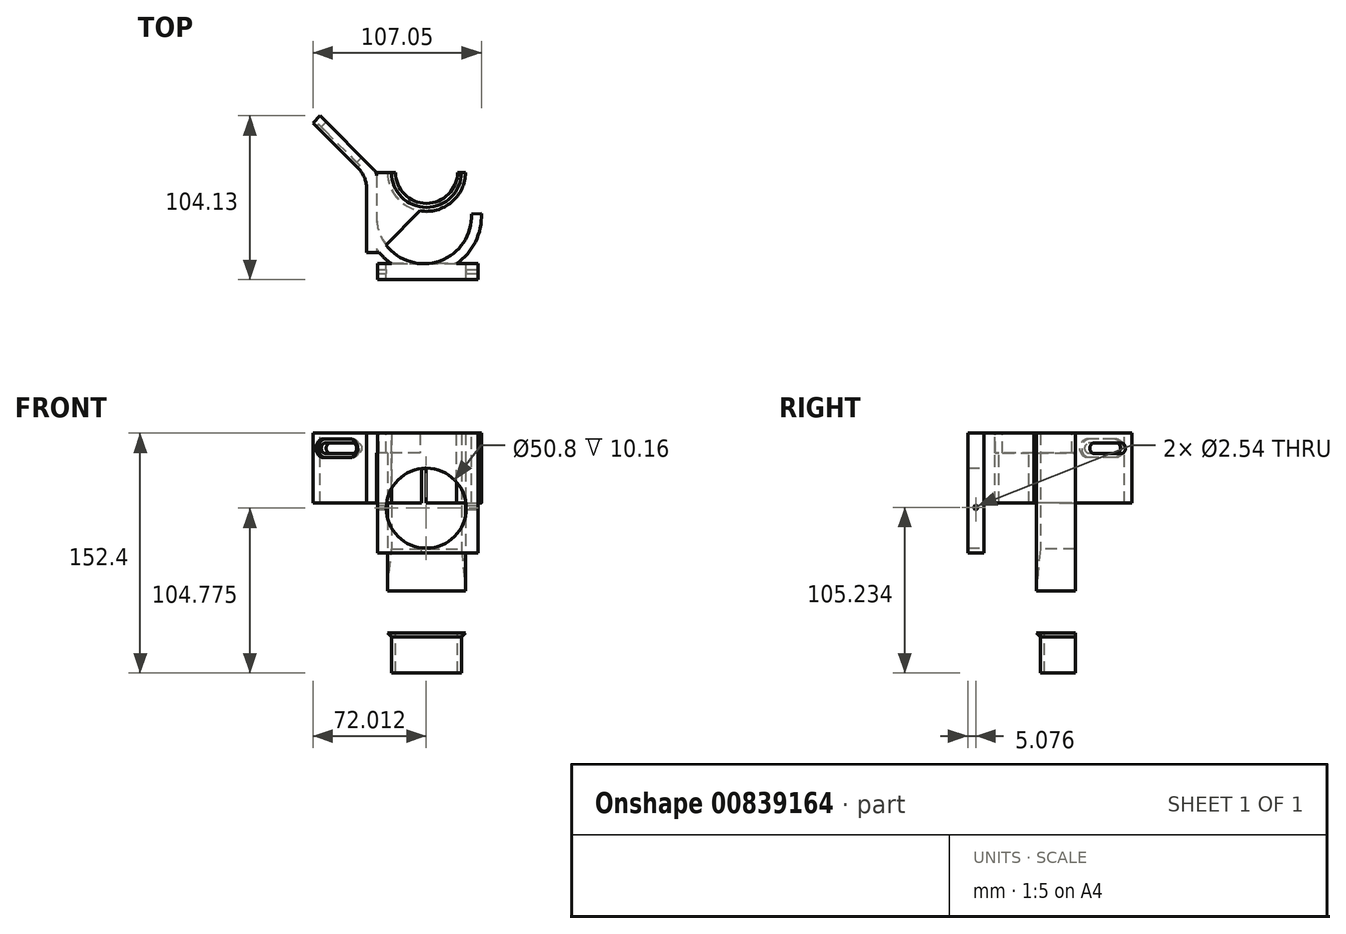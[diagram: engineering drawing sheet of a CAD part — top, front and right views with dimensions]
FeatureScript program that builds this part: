
annotation { "Feature Type Name" : "Feature", "Feature Type Description" : "" }
export const myFeature = defineFeature(function(context is Context, id is Id, definition is map)
    precondition{}
    {
        {
            var Q0;
            Q0=qCreatedBy(makeId("Top.planeOp"),FACE);
            var sketch = newSketch(context, id + "F0", { "sketchPlane" : qUnion([Q0])});
            skCircle(sketch, "E0", {"center": v(0, 0) * mm, "radius": 22.23 * mm});
            skCircle(sketch, "E1", {"center": v(0, 0) * mm, "radius": 24.77 * mm});
            skSolve(sketch);
        }
        {
            var Q0;
            Q0=makeQuery(id+"F0.imprint","IMPRINT",FACE,{"disambiguationData":[TD([[makeQuery(id+"F0.imprint","IMPRINT",EDGE,{"derivedFrom":sQuery(id+"F0.wireOp",EDGE,"E0")}),-1.0]])]});
            var sketch = newSketch(context, id + "F1", { "sketchPlane" : qUnion([Q0])});
            skSolve(sketch);
        }
        {
            var Q0;
            Q0=makeQuery(id+"F1.imprint","IMPRINT",FACE,{"disambiguationData":[TD([[makeQuery(id+"F1.imprint","IMPRINT",EDGE,{"derivedFrom":makeQuery(id+"F0.imprint","IMPRINT",EDGE,{"derivedFrom":sQuery(id+"F0.wireOp",EDGE,"E0")})}),-1.0]])]});
            extrude(context, id + "F2", {"entities" : qUnion([Q0]), "depth" : 127 * mm, "offsetDistance" : 25.4 * mm});
        }
        {
            var Q0;
            Q0=qCreatedBy(makeId("Top.planeOp"),FACE);
            var sketch = newSketch(context, id + "F3", { "sketchPlane" : qUnion([Q0])});
            skLineSegment(sketch, "E2.bottom", {"start": v(38.25, 0) * mm, "end": v(-119.23, 0) * mm});
            skLineSegment(sketch, "E2.top", {"start": v(38.25, 78.16) * mm, "end": v(-119.23, 78.16) * mm});
            skLineSegment(sketch, "E2.left", {"start": v(38.25, 0) * mm, "end": v(38.25, 78.16) * mm});
            skLineSegment(sketch, "E2.right", {"start": v(-119.23, 0) * mm, "end": v(-119.23, 78.16) * mm});
            skPoint(sketch, "E2.middle", {"position": v(-40.5, 39.08) * mm});
            skSolve(sketch);
        }
        {
            var Q0;
            Q0=makeQuery(id+"F3.imprint","IMPRINT",FACE,{"disambiguationData":[TD([[makeQuery(id+"F3.imprint","IMPRINT",EDGE,{"derivedFrom":sQuery(id+"F3.wireOp",EDGE,"E2.bottom")}),-1.0]])]});
            extrude(context, id + "F4", {"entities" : qUnion([Q0]), "operationType" : NewBodyOperationType.REMOVE, "endBound" : BoundingType.SYMMETRIC, "oppositeDirection" : true, "depth" : 508 * mm, "offsetDistance" : 25.4 * mm});
        }
        {
            var Q0;
            Q0=qCreatedBy(makeId("Top.planeOp"),FACE);
            cPlane(context, id + "F5", {"entities" : qUnion([Q0]), "cplaneType" : CPlaneType.OFFSET, "offset" : 50.8 * mm, "width" : 152.4 * mm, "height" : 152.4 * mm});
        }
        {
            var Q0;
            Q0=qCreatedBy(makeId("Top.planeOp"),FACE);
            var sketch = newSketch(context, id + "F6", { "sketchPlane" : qUnion([Q0])});
            skArc(sketch, "E3.0", {"start": v(-22.23, 0) * mm, "mid": v(0, -22.23) * mm, "end": v(22.23, 0) * mm});
            skArc(sketch, "E4.0", {"start": v(-19.69, 0) * mm, "mid": v(0, -19.69) * mm, "end": v(19.69, 0) * mm});
            skLineSegment(sketch, "E5", {"start": v(19.69, 0) * mm, "end": v(22.23, 0) * mm});
            skLineSegment(sketch, "E6", {"start": v(22.23, 0) * mm, "end": v(-19.69, 0) * mm});
            skLineSegment(sketch, "E7", {"start": v(-19.69, 0) * mm, "end": v(-22.23, 0) * mm});
            skSolve(sketch);
        }
        {
            var Q0;
            Q0=makeQuery(id+"F6.imprint","IMPRINT",FACE,{"disambiguationData":[TD([[makeQuery(id+"F6.imprint","IMPRINT",EDGE,{"derivedFrom":sQuery(id+"F6.wireOp",EDGE,"E3.0")}),1.0]])]});
            extrude(context, id + "F7", {"entities" : qUnion([Q0]), "oppositeDirection" : true, "depth" : 25.4 * mm, "offsetDistance" : 25.4 * mm});
        }
        {
            var Q0;
            Q0=qCreatedBy(makeId("Front.planeOp"),FACE);
            var sketch = newSketch(context, id + "F8", { "sketchPlane" : qUnion([Q0])});
            skLineSegment(sketch, "E8.0", {"start": v(22.23, 0) * mm, "end": v(24.77, 0) * mm});
            skLineSegment(sketch, "E9.0", {"start": v(22.23, -2.54) * mm, "end": v(22.23, 0) * mm});
            skPoint(sketch, "E10.orphan", {"position": v(-24.77, 0) * mm});
            skLineSegment(sketch, "E11", {"start": v(24.77, 0) * mm, "end": v(22.23, -2.54) * mm});
            skPoint(sketch, "E12.orphan", {"position": v(22.23, -25.4) * mm});
            skSolve(sketch);
        }
        {
            var Q0;
            Q0=makeQuery(id+"F8.imprint","IMPRINT",FACE,{"disambiguationData":[TD([[makeQuery(id+"F8.imprint","IMPRINT",EDGE,{"derivedFrom":sQuery(id+"F8.wireOp",EDGE,"E8.0")}),-1.0]])]});
            var Q1;
            Q1=makeQuery(id+"F7.opExtrude","SWEPT_FACE",FACE,{"disambiguationData":[OSD([sQuery(id+"F6.wireOp",EDGE,"E4.0")])]});
            revolve(context, id + "F9", {"surfaceOperationType" : NewSurfaceOperationType.NEW, "entities" : qUnion([Q0]), "axis" : qUnion([Q1]), "revolveType" : RevolveType.ONE_DIRECTION, "angle" : 180 * degree});
        }
        {
            var Q0;
            Q0=makeQuery(id+"F2.opExtrude","CAP_EDGE",EDGE,{"disambiguationData":[OSD([sQuery(id+"F0.wireOp",EDGE,"E0")])],"isStart":true});
            chamfer(context, id + "F10", {"entities" : qUnion([Q0]), "chamferType" : ChamferType.TWO_OFFSETS, "width1" : 5.08 * mm, "oppositeDirection" : false, "width2" : 53.34 * mm, "tangentPropagation" : true});
        }
        {
            var Q0;
            Q0=qCreatedBy(makeId("Right.planeOp"),FACE);
            cPlane(context, id + "F11", {"entities" : qUnion([Q0]), "cplaneType" : CPlaneType.OFFSET, "offset" : 31.75 * mm, "oppositeDirection" : true, "width" : 152.4 * mm, "height" : 152.4 * mm});
        }
        {
            var Q0;
            Q0=qCreatedBy(id+"F11.planeOp",FACE);
            var sketch = newSketch(context, id + "F12", { "sketchPlane" : qUnion([Q0])});
            skLineSegment(sketch, "E13.bottom", {"start": v(0, 127) * mm, "end": v(-50.8, 127) * mm});
            skLineSegment(sketch, "E13.top", {"start": v(0, 114.3) * mm, "end": v(-50.8, 114.3) * mm});
            skLineSegment(sketch, "E13.left", {"start": v(0, 127) * mm, "end": v(0, 114.3) * mm});
            skLineSegment(sketch, "E13.right", {"start": v(-50.8, 127) * mm, "end": v(-50.8, 114.3) * mm});
            skSolve(sketch);
        }
        {
            var Q0;
            Q0=makeQuery(id+"F12.imprint","IMPRINT",FACE,{"disambiguationData":[TD([[makeQuery(id+"F12.imprint","IMPRINT",EDGE,{"derivedFrom":sQuery(id+"F12.wireOp",EDGE,"E13.bottom")}),1.0]])]});
            var Q1;
            Q1=makeQuery(id+"F2.opExtrude","SWEPT_FACE",FACE,{"disambiguationData":[OSD([sQuery(id+"F0.wireOp",EDGE,"E1")])]});
            var Q2;
            Q2=makeQuery(id+"F2.opExtrude","SWEPT_BODY",BODY,{"disambiguationData":[OSD([sQuery(id+"F0.wireOp",EDGE,"E0"),sQuery(id+"F0.wireOp",EDGE,"E1")])]});
            extrude(context, id + "F13", {"entities" : qUnion([Q0]), "operationType" : NewBodyOperationType.ADD, "depth" : 31.75 * mm, "endBoundEntityFace" : qUnion([Q1]), "endBoundEntityBody" : qUnion([Q2]), "offsetDistance" : 25.4 * mm});
        }
        {
            var Q0;
            Q0=makeQuery(id+"F13.boolean.opBoolean","MERGE",FACE,{"derivedFrom":[makeQuery(id+"F2.opExtrude","CAP_FACE",FACE,{"disambiguationData":[OSD([sQuery(id+"F0.wireOp",EDGE,"E0"),sQuery(id+"F0.wireOp",EDGE,"E1")])],"isStart":false}),makeQuery(id+"F13.opExtrude","SWEPT_FACE",FACE,{"disambiguationData":[OSD([sQuery(id+"F12.wireOp",EDGE,"E13.bottom")])]})]});
            var sketch = newSketch(context, id + "F14", { "sketchPlane" : qUnion([Q0])});
            skCircle(sketch, "E14", {"center": v(0, 0) * mm, "radius": 22.23 * mm});
            skSolve(sketch);
        }
        {
            var Q0;
            {var subQ0=sQuery(id+"F14.wireOp",EDGE,"E14");var subQ1=makeQuery(id+"F4.opExtrude","SWEPT_FACE",FACE,{"disambiguationData":[OSD([sQuery(id+"F3.wireOp",EDGE,"E2.bottom")])]});var subQ2=sQuery(id+"F0.wireOp",EDGE,"E0");var subQ3=makeQuery(id+"F2.opExtrude","CAP_FACE",FACE,{"disambiguationData":[OSD([subQ2,sQuery(id+"F0.wireOp",EDGE,"E1")])],"isStart":false});var subQ4=makeQuery(id+"F14.imprint","INTERSECT",VERTEX,{"derivedFrom":[makeQuery(id+"F4.boolean.opBoolean","INTERSECT",EDGE,{"disambiguationData":[OD(1.0)],"derivedFrom":[subQ3,subQ1]}),subQ0]});Q0=makeQuery(id+"F14.imprint","IMPRINT",FACE,{"disambiguationData":[TD([[makeQuery(id+"F14.imprint","IMPRINT",EDGE,{"disambiguationData":[TD([[subQ4,-1.0]])],"derivedFrom":subQ0}),1.0]])]});}
            var Q1;
            {var subQ2=sQuery(id+"F0.wireOp",EDGE,"E0");var subQ4=sQuery(id+"F12.wireOp",EDGE,"E13.bottom");var subQ6=makeQuery(id+"F13.boolean.opBoolean","SPLIT",EDGE,{"disambiguationData":[TD([makeQuery(id+"F2.opExtrude","SWEPT_FACE",FACE,{"disambiguationData":[OSD([subQ2])]})])],"derivedFrom":makeQuery(id+"F13.opExtrude","CAP_EDGE",EDGE,{"disambiguationData":[OSD([subQ4])],"isStart":false})});Q1=makeQuery(id+"F14.imprint","IMPRINT",FACE,{"disambiguationData":[TD([[makeQuery(id+"F14.imprint","IMPRINT",EDGE,{"derivedFrom":subQ6}),-1.0]])]});}
            extrude(context, id + "F15", {"entities" : qUnion([Q0, Q1]), "operationType" : NewBodyOperationType.REMOVE, "oppositeDirection" : true, "depth" : 15.24 * mm, "offsetDistance" : 25.4 * mm});
        }
        {
            var Q0;
            Q0=makeQuery(id+"F13.opExtrude","CAP_EDGE",EDGE,{"disambiguationData":[OSD([sQuery(id+"F12.wireOp",EDGE,"E13.right")])],"isStart":false});
            chamfer(context, id + "F16", {"entities" : qUnion([Q0]), "width" : 30.48 * mm, "tangentPropagation" : true});
        }
        {
            var Q0;
            Q0=makeQuery(id+"F13.boolean.opBoolean","MERGE",FACE,{"derivedFrom":[makeQuery(id+"F2.opExtrude","CAP_FACE",FACE,{"disambiguationData":[OSD([sQuery(id+"F0.wireOp",EDGE,"E0"),sQuery(id+"F0.wireOp",EDGE,"E1")])],"isStart":false}),makeQuery(id+"F13.opExtrude","SWEPT_FACE",FACE,{"disambiguationData":[OSD([sQuery(id+"F12.wireOp",EDGE,"E13.bottom")])]})]});
            var sketch = newSketch(context, id + "F17", { "sketchPlane" : qUnion([Q0])});
            skLineSegment(sketch, "E15.0", {"start": v(-31.75, 0) * mm, "end": v(-31.75, -50.8) * mm});
            skLineSegment(sketch, "E16", {"start": v(-31.75, 0) * mm, "end": v(-67.67, 35.92) * mm});
            skLineSegment(sketch, "E17.0", {"start": v(-38.1, -2.63) * mm, "end": v(-72.16, 31.43) * mm});
            skLineSegment(sketch, "E18.0", {"start": v(-38.1, -2.63) * mm, "end": v(-38.1, -50.8) * mm});
            skLineSegment(sketch, "E19", {"start": v(-31.75, -50.8) * mm, "end": v(-38.1, -50.8) * mm});
            skLineSegment(sketch, "E20", {"start": v(-67.67, 35.92) * mm, "end": v(-72.16, 31.43) * mm});
            skSolve(sketch);
        }
        {
            var Q0;
            Q0=makeQuery(id+"F17.imprint","IMPRINT",FACE,{"disambiguationData":[TD([[makeQuery(id+"F17.imprint","IMPRINT",EDGE,{"derivedFrom":sQuery(id+"F17.wireOp",EDGE,"E15.0")}),-1.0]])]});
            extrude(context, id + "F18", {"entities" : qUnion([Q0]), "oppositeDirection" : true, "depth" : 19.05 * mm, "offsetDistance" : 25.4 * mm});
        }
        {
            var Q0;
            Q0=makeQuery(id+"F18.opExtrude","SWEPT_FACE",FACE,{"disambiguationData":[OSD([sQuery(id+"F17.wireOp",EDGE,"E17.0")])]});
            var sketch = newSketch(context, id + "F19", { "sketchPlane" : qUnion([Q0])});
            skLineSegment(sketch, "E21.bottom", {"start": v(-64.36, 111.68) * mm, "end": v(-38.96, 111.68) * mm});
            skLineSegment(sketch, "E21.top", {"start": v(-64.36, 123.24) * mm, "end": v(-38.96, 123.24) * mm});
            skArc(sketch, "E22", {"start": v(-38.96, 111.68) * mm, "mid": v(-33.18, 117.46) * mm, "end": v(-38.96, 123.24) * mm});
            skArc(sketch, "E23", {"start": v(-64.36, 123.24) * mm, "mid": v(-70.14, 117.46) * mm, "end": v(-64.36, 111.68) * mm});
            skLineSegment(sketch, "E24.0", {"start": v(-64.36, 114.22) * mm, "end": v(-38.96, 114.22) * mm});
            skArc(sketch, "E24.1", {"start": v(-64.36, 120.7) * mm, "mid": v(-67.6, 117.46) * mm, "end": v(-64.36, 114.22) * mm});
            skLineSegment(sketch, "E24.2", {"start": v(-64.36, 120.7) * mm, "end": v(-38.96, 120.7) * mm});
            skArc(sketch, "E24.3", {"start": v(-38.96, 114.22) * mm, "mid": v(-35.72, 117.46) * mm, "end": v(-38.96, 120.7) * mm});
            skSolve(sketch);
        }
        {
            var Q0;
            Q0=makeQuery(id+"F19.imprint","IMPRINT",FACE,{"disambiguationData":[TD([[makeQuery(id+"F19.imprint","IMPRINT",EDGE,{"derivedFrom":sQuery(id+"F19.wireOp",EDGE,"E24.0")}),1.0]])]});
            extrude(context, id + "F20", {"entities" : qUnion([Q0]), "operationType" : NewBodyOperationType.REMOVE, "oppositeDirection" : true, "depth" : 25.4 * mm, "offsetDistance" : 25.4 * mm});
        }
        {
            var Q0;
            Q0=makeQuery(id+"F19.imprint","IMPRINT",FACE,{"disambiguationData":[TD([[makeQuery(id+"F19.imprint","IMPRINT",EDGE,{"derivedFrom":sQuery(id+"F19.wireOp",EDGE,"E21.bottom")}),1.0]])]});
            extrude(context, id + "F21", {"entities" : qUnion([Q0]), "operationType" : NewBodyOperationType.REMOVE, "oppositeDirection" : true, "depth" : 1.9 * mm, "offsetDistance" : 25.4 * mm});
        }
        {
            var Q0;
            Q0=makeQuery(id+"F18.opExtrude","SWEPT_EDGE",EDGE,{"disambiguationData":[OSD([sQuery(id+"F17.wireOp",EDGE,"E17.0"),sQuery(id+"F17.wireOp",EDGE,"E18.0")])]});
            fillet(context, id + "F22", {"entities" : qUnion([Q0]), "radius" : 17.78 * mm, "tangentPropagation" : true, "allowEdgeOverflow" : false});
        }
        {
            var Q0;
            Q0=makeQuery(id+"F18.opExtrude","SWEPT_EDGE",EDGE,{"disambiguationData":[OSD([sQuery(id+"F0.wireOp",EDGE,"E0"),sQuery(id+"F0.wireOp",EDGE,"E1"),sQuery(id+"F3.wireOp",EDGE,"E2.bottom"),sQuery(id+"F12.wireOp",EDGE,"E13.bottom"),sQuery(id+"F12.wireOp",EDGE,"E13.left"),sQuery(id+"F17.wireOp",EDGE,"E15.0"),sQuery(id+"F17.wireOp",EDGE,"E16")])]});
            fillet(context, id + "F23", {"entities" : qUnion([Q0]), "radius" : 5.08 * mm, "tangentPropagation" : true, "allowEdgeOverflow" : false});
        }
        {
            var Q0;
            Q0=makeQuery(id+"F18.opExtrude","CAP_FACE",FACE,{"disambiguationData":[OSD([sQuery(id+"F17.wireOp",EDGE,"E15.0"),sQuery(id+"F17.wireOp",EDGE,"E17.0"),sQuery(id+"F17.wireOp",EDGE,"E18.0"),sQuery(id+"F17.wireOp",EDGE,"E16"),sQuery(id+"F17.wireOp",EDGE,"E19"),sQuery(id+"F17.wireOp",EDGE,"E20")])],"isStart":true});
            var sketch = newSketch(context, id + "F24", { "sketchPlane" : qUnion([Q0])});
            skArc(sketch, "E25", {"start": v(-31.75, -26.45) * mm, "mid": v(-1.62, -58.1) * mm, "end": v(28.5, -26.45) * mm});
            skPoint(sketch, "E25.endSnap0", {"position": v(-31.75, -26.45) * mm});
            skArc(sketch, "E26.0", {"start": v(-38.1, -26.14) * mm, "mid": v(-1.62, -64.44) * mm, "end": v(34.85, -26.14) * mm});
            skLineSegment(sketch, "E27", {"start": v(34.85, -26.14) * mm, "end": v(28.5, -26.45) * mm});
            skLineSegment(sketch, "E28", {"start": v(-31.75, -26.45) * mm, "end": v(-38.1, -26.14) * mm});
            skSolve(sketch);
        }
        {
            var Q0;
            {var subQ0=sQuery(id+"F24.wireOp",EDGE,"E27");Q0=makeQuery(id+"F24.imprint","IMPRINT",FACE,{"disambiguationData":[TD([[makeQuery(id+"F24.imprint","IMPRINT",EDGE,{"derivedFrom":subQ0}),1.0]])]});}
            var Q1;
            Q1=makeQuery(id+"F18.opExtrude","CAP_FACE",FACE,{"disambiguationData":[OSD([sQuery(id+"F17.wireOp",EDGE,"E15.0"),sQuery(id+"F17.wireOp",EDGE,"E17.0"),sQuery(id+"F17.wireOp",EDGE,"E18.0"),sQuery(id+"F17.wireOp",EDGE,"E16"),sQuery(id+"F17.wireOp",EDGE,"E19"),sQuery(id+"F17.wireOp",EDGE,"E20")])],"isStart":false});
            extrude(context, id + "F25", {"entities" : qUnion([Q0]), "operationType" : NewBodyOperationType.ADD, "endBound" : BoundingType.UP_TO_SURFACE, "oppositeDirection" : true, "depth" : 25.4 * mm, "endBoundEntityFace" : qUnion([Q1]), "offsetDistance" : 25.4 * mm});
        }
        {
            var Q0;
            {var subQ0=sQuery(id+"F17.wireOp",EDGE,"E15.0");Q0=makeQuery(id+"F25.boolean.opBoolean","MERGE",FACE,{"derivedFrom":[makeQuery(id+"F18.opExtrude","CAP_FACE",FACE,{"disambiguationData":[OSD([subQ0,sQuery(id+"F17.wireOp",EDGE,"E17.0"),sQuery(id+"F17.wireOp",EDGE,"E18.0"),sQuery(id+"F17.wireOp",EDGE,"E16"),sQuery(id+"F17.wireOp",EDGE,"E19"),sQuery(id+"F17.wireOp",EDGE,"E20")])],"isStart":true}),makeQuery(id+"F25.opExtrude","CAP_FACE",FACE,{"disambiguationData":[OSD([subQ0,sQuery(id+"F24.wireOp",EDGE,"E25"),sQuery(id+"F24.wireOp",EDGE,"E26.0"),sQuery(id+"F24.wireOp",EDGE,"E27")])],"isStart":true})]});}
            var sketch = newSketch(context, id + "F26", { "sketchPlane" : qUnion([Q0])});
            skPoint(sketch, "E29.firstSnap0", {"position": v(-0.15, -58.05) * mm});
            skLineSegment(sketch, "E29.bottom", {"start": v(-31.13, -58.05) * mm, "end": v(32.88, -58.05) * mm});
            skLineSegment(sketch, "E29.top", {"start": v(-31.13, -68.21) * mm, "end": v(32.88, -68.21) * mm});
            skLineSegment(sketch, "E29.left", {"start": v(-31.13, -58.05) * mm, "end": v(-31.13, -68.21) * mm});
            skLineSegment(sketch, "E29.right", {"start": v(32.88, -58.05) * mm, "end": v(32.88, -68.21) * mm});
            skSolve(sketch);
        }
        {
            var Q0;
            {var subQ0=sQuery(id+"F26.wireOp",EDGE,"E29.right");Q0=makeQuery(id+"F26.imprint","IMPRINT",FACE,{"disambiguationData":[TD([[makeQuery(id+"F26.imprint","IMPRINT",EDGE,{"derivedFrom":subQ0}),-1.0]])]});}
            var Q1;
            {var subQ0=sQuery(id+"F26.wireOp",EDGE,"E29.bottom");var subQ4=makeQuery(id+"F25.opExtrude","CAP_EDGE",EDGE,{"disambiguationData":[OSD([sQuery(id+"F24.wireOp",EDGE,"E26.0")])],"isStart":true});var subQ9=makeQuery(id+"F26.imprint","INTERSECT",VERTEX,{"disambiguationData":[OD(0.0)],"derivedFrom":[subQ4,subQ0]});Q1=makeQuery(id+"F26.imprint","IMPRINT",FACE,{"disambiguationData":[TD([[makeQuery(id+"F26.imprint","IMPRINT",EDGE,{"disambiguationData":[TD([[subQ9,-1.0]])],"derivedFrom":subQ0}),-1.0]])]});}
            var Q2;
            {var subQ0=sQuery(id+"F26.wireOp",EDGE,"E29.left");Q2=makeQuery(id+"F26.imprint","IMPRINT",FACE,{"disambiguationData":[TD([[makeQuery(id+"F26.imprint","IMPRINT",EDGE,{"derivedFrom":subQ0}),1.0]])]});}
            extrude(context, id + "F27", {"entities" : qUnion([Q0, Q1, Q2]), "operationType" : NewBodyOperationType.ADD, "oppositeDirection" : true, "depth" : 76.2 * mm, "offsetDistance" : 25.4 * mm});
        }
        {
            var Q0;
            {var subQ0=sQuery(id+"F26.wireOp",EDGE,"E29.bottom");Q0=makeQuery(id+"F27.opExtrude","SWEPT_FACE",FACE,{"disambiguationData":[OSD([subQ0]),TDD([makeQuery(id+"F26.imprint","IMPRINT",EDGE,{"disambiguationData":[TD([[makeQuery(id+"F26.imprint","INTERSECT",VERTEX,{"disambiguationData":[OD(1.0)],"derivedFrom":[makeQuery(id+"F25.opExtrude","CAP_EDGE",EDGE,{"disambiguationData":[OSD([sQuery(id+"F24.wireOp",EDGE,"E25")])],"isStart":true}),subQ0]}),-1.0]])],"derivedFrom":subQ0}),makeQuery(id+"F26.imprint","IMPRINT",EDGE,{"disambiguationData":[TD([[makeQuery(id+"F26.imprint","INTERSECT",VERTEX,{"derivedFrom":[subQ0,sQuery(id+"F26.wireOp",EDGE,"E29.right")]}),1.0]])],"derivedFrom":subQ0})])]});}
            var sketch = newSketch(context, id + "F28", { "sketchPlane" : qUnion([Q0])});
            skCircle(sketch, "E30", {"center": v(0.15, 79.37) * mm, "radius": 25.4 * mm});
            skSolve(sketch);
        }
        {
            var Q0;
            {var subQ0=sQuery(id+"F28.wireOp",EDGE,"E30");var subQ1=sQuery(id+"F26.wireOp",EDGE,"E29.bottom");var subQ2=sQuery(id+"F24.wireOp",EDGE,"E25");var subQ3=makeQuery(id+"F27.opExtrude","SWEPT_EDGE",EDGE,{"disambiguationData":[OSD([subQ2,subQ1]),TDD([makeQuery(id+"F26.imprint","INTERSECT",VERTEX,{"disambiguationData":[OD(1.0)],"derivedFrom":[makeQuery(id+"F25.opExtrude","CAP_EDGE",EDGE,{"disambiguationData":[OSD([subQ2])],"isStart":true}),subQ1]})])]});var subQ4=makeQuery(id+"F28.imprint","INTERSECT",VERTEX,{"disambiguationData":[OD(0.0)],"derivedFrom":[subQ3,subQ0]});Q0=makeQuery(id+"F28.imprint","IMPRINT",FACE,{"disambiguationData":[TD([[makeQuery(id+"F28.imprint","IMPRINT",EDGE,{"disambiguationData":[TD([[subQ4,1.0]])],"derivedFrom":subQ0}),1.0]])]});}
            var Q1;
            {var subQ0=sQuery(id+"F28.wireOp",EDGE,"E30");var subQ1=sQuery(id+"F26.wireOp",EDGE,"E29.bottom");var subQ2=sQuery(id+"F24.wireOp",EDGE,"E25");var subQ3=makeQuery(id+"F27.opExtrude","SWEPT_EDGE",EDGE,{"disambiguationData":[OSD([subQ2,subQ1]),TDD([makeQuery(id+"F26.imprint","INTERSECT",VERTEX,{"disambiguationData":[OD(1.0)],"derivedFrom":[makeQuery(id+"F25.opExtrude","CAP_EDGE",EDGE,{"disambiguationData":[OSD([subQ2])],"isStart":true}),subQ1]})])]});var subQ4=makeQuery(id+"F28.imprint","INTERSECT",VERTEX,{"disambiguationData":[OD(0.0)],"derivedFrom":[subQ3,subQ0]});Q1=makeQuery(id+"F28.imprint","IMPRINT",FACE,{"disambiguationData":[TD([[makeQuery(id+"F28.imprint","IMPRINT",EDGE,{"disambiguationData":[TD([[subQ4,-1.0]])],"derivedFrom":subQ0}),1.0]])]});}
            extrude(context, id + "F29", {"entities" : qUnion([Q0, Q1]), "operationType" : NewBodyOperationType.REMOVE, "oppositeDirection" : true, "depth" : 25.4 * mm, "offsetDistance" : 25.4 * mm});
        }
        {
            var Q0;
            Q0=makeQuery(id+"F27.opExtrude","SWEPT_FACE",FACE,{"disambiguationData":[OSD([sQuery(id+"F26.wireOp",EDGE,"E29.right")])]});
            var sketch = newSketch(context, id + "F30", { "sketchPlane" : qUnion([Q0])});
            skCircle(sketch, "E31", {"center": v(-63.13, 79.83) * mm, "radius": 1.27 * mm});
            skSolve(sketch);
        }
        {
            var Q0;
            Q0=makeQuery(id+"F30.imprint","IMPRINT",FACE,{"disambiguationData":[TD([[makeQuery(id+"F30.imprint","IMPRINT",EDGE,{"derivedFrom":sQuery(id+"F30.wireOp",EDGE,"E31")}),1.0]])]});
            extrude(context, id + "F31", {"entities" : qUnion([Q0]), "operationType" : NewBodyOperationType.REMOVE, "oppositeDirection" : true, "depth" : 127 * mm, "offsetDistance" : 25.4 * mm});
        }
        {
            var Q0;
            {var subQ1=sQuery(id+"F17.wireOp",EDGE,"E17.0");var subQ2=sQuery(id+"F17.wireOp",EDGE,"E16");var subQ3=sQuery(id+"F17.wireOp",EDGE,"E15.0");var subQ4=sQuery(id+"F17.wireOp",EDGE,"E20");var subQ5=sQuery(id+"F17.wireOp",EDGE,"E19");var subQ7=sQuery(id+"F17.wireOp",EDGE,"E18.0");Q0=makeQuery(id+"F27.boolean.opBoolean","SPLIT",FACE,{"disambiguationData":[TD([makeQuery(id+"F18.opExtrude","SWEPT_FACE",FACE,{"disambiguationData":[OSD([subQ3])]})])],"derivedFrom":makeQuery(id+"F25.boolean.opBoolean","MERGE",FACE,{"derivedFrom":[makeQuery(id+"F18.opExtrude","CAP_FACE",FACE,{"disambiguationData":[OSD([subQ3,subQ1,subQ7,subQ2,subQ5,subQ4])],"isStart":false}),makeQuery(id+"F25.opExtrude","CAP_FACE",FACE,{"disambiguationData":[OSD([subQ3,subQ1,subQ7,subQ2,subQ5,subQ4])],"isStart":false})]})});}
            var Q1;
            {var subQ4=sQuery(id+"F17.wireOp",EDGE,"E20");var subQ5=sQuery(id+"F17.wireOp",EDGE,"E19");var subQ6=sQuery(id+"F17.wireOp",EDGE,"E16");var subQ7=sQuery(id+"F17.wireOp",EDGE,"E18.0");var subQ8=sQuery(id+"F17.wireOp",EDGE,"E17.0");var subQ9=sQuery(id+"F17.wireOp",EDGE,"E15.0");Q1=makeQuery(id+"F27.boolean.opBoolean","SPLIT",FACE,{"disambiguationData":[TD([makeQuery(id+"F25.opExtrude","SWEPT_FACE",FACE,{"disambiguationData":[OSD([sQuery(id+"F24.wireOp",EDGE,"E27")])]})])],"derivedFrom":makeQuery(id+"F25.boolean.opBoolean","MERGE",FACE,{"derivedFrom":[makeQuery(id+"F18.opExtrude","CAP_FACE",FACE,{"disambiguationData":[OSD([subQ9,subQ8,subQ7,subQ6,subQ5,subQ4])],"isStart":false}),makeQuery(id+"F25.opExtrude","CAP_FACE",FACE,{"disambiguationData":[OSD([subQ9,subQ8,subQ7,subQ6,subQ5,subQ4])],"isStart":false})]})});}
            extrude(context, id + "F32", {"entities" : qUnion([Q0, Q1]), "operationType" : NewBodyOperationType.ADD, "depth" : 25.4 * mm, "offsetDistance" : 25.4 * mm});
        }
    });
